# Revit family: LDA_BIM_TECLADO EXPANSIÓN_VAP-8K
name_source: partatom
category: Equipos especializados
units: mm (PartAtom-declared; Revit-internal decimal feet)

## family parameters
Compartido = No
Corte con vacíos al cargar = No
Cota de conector redondo = Diámetro de uso
Punto de cálculo de habitación = No
Se basa en plano de trabajo = No
Siempre vertical = Sí
Tipo de pieza = Normal

## types (1)
- LDA_BIM_TECLADO EXPANSIÓN_VAP-8K
    Acabado = Fe, Gris RAL 7016
    Botones = 8 x selección de zona
    Condiciones de Funcionamiento = 5 ºC to +45 ºC / 23 ºF to 113 ºF // 5% to 95% Humedad Relativa (sin condensación)
    Descripción = El VAP 8K es un teclado de expansión para el panel de alarma por voz VAP 1.
    Elevación por defecto = 0 mm  [stored 0 ft]
    Fabricante = LDA
    Modelo = VAP-8K
    Peso = 0,85 Kg
    Referencia = LDAVAP8KS01
    Tipo de transductor = Condensador
    URL = https://support.lda-audiotech.com

note: [stored X ft] marks values corroborated as IEEE doubles in the binary element streams (Revit-internal decimal feet)

## geometry (parser evidence)
native form markers: Sweep x2
no freeform markers — native parametric forms only
